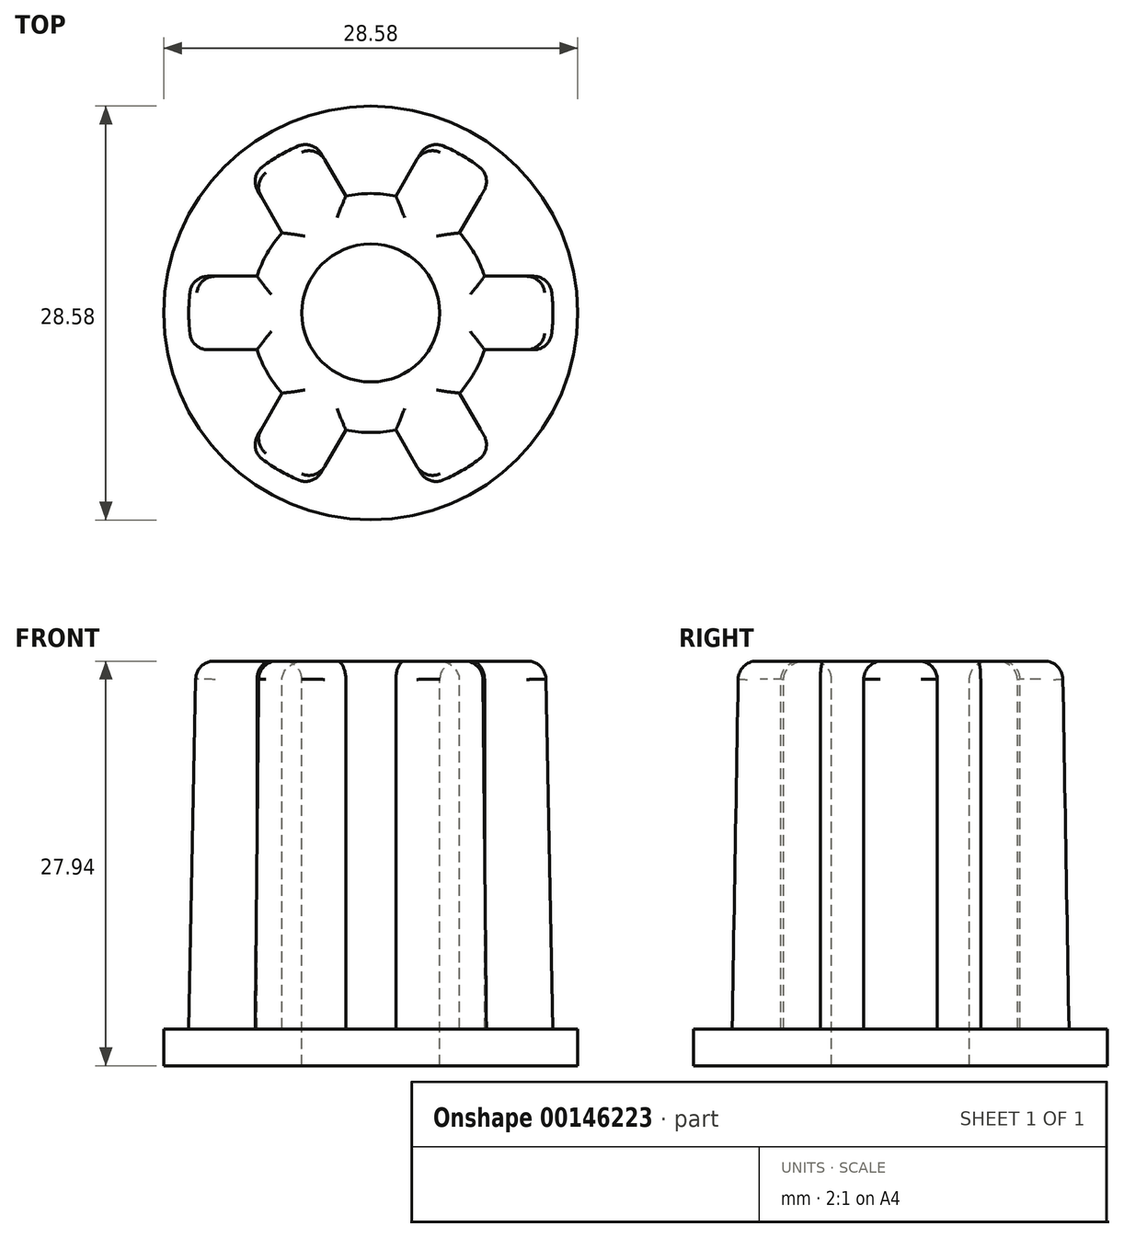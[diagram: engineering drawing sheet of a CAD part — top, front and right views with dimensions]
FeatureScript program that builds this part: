
annotation { "Feature Type Name" : "Feature", "Feature Type Description" : "" }
export const myFeature = defineFeature(function(context is Context, id is Id, definition is map)
    precondition{}
    {
        {
            var Q0;
            Q0=qCreatedBy(makeId("Top.planeOp"),FACE);
            var sketch = newSketch(context, id + "F0", { "sketchPlane" : qUnion([Q0])});
            skCircle(sketch, "E0", {"center": v(0, 0) * mm, "radius": 12.57 * mm});
            skSolve(sketch);
        }
        {
            var Q0;
            Q0=qCreatedBy(makeId("Top.planeOp"),FACE);
            cPlane(context, id + "F1", {"entities" : qUnion([Q0]), "cplaneType" : CPlaneType.OFFSET, "offset" : 25.4 * mm, "width" : 152.4 * mm, "height" : 152.4 * mm});
        }
        {
            var Q0;
            Q0=qCreatedBy(id+"F1.planeOp",FACE);
            var sketch = newSketch(context, id + "F2", { "sketchPlane" : qUnion([Q0])});
            skCircle(sketch, "E1", {"center": v(0, 0) * mm, "radius": 12.07 * mm});
            skSolve(sketch);
        }
        {
            var Q0;
            Q0=makeQuery(id+"F0.imprint","IMPRINT",FACE,{"disambiguationData":[TD([[makeQuery(id+"F0.imprint","IMPRINT",EDGE,{"derivedFrom":sQuery(id+"F0.wireOp",EDGE,"E0")}),1.0]])]});
            var Q1;
            Q1=makeQuery(id+"F2.imprint","IMPRINT",FACE,{"disambiguationData":[TD([[makeQuery(id+"F2.imprint","IMPRINT",EDGE,{"derivedFrom":sQuery(id+"F2.wireOp",EDGE,"E1")}),1.0]])]});
            loft(context, id + "F3", {"sheetProfilesArray" : [{ "sheetProfileEntities" : qUnion([Q0]) }, { "sheetProfileEntities" : qUnion([Q1]) }]});
        }
        {
            var Q0;
            Q0=makeQuery(id+"F3.opLoft","CAP_FACE",FACE,{"disambiguationData":[OSD([makeQuery(id+"F0.imprint","IMPRINT",FACE,{"disambiguationData":[TD([[makeQuery(id+"F0.imprint","IMPRINT",EDGE,{"derivedFrom":sQuery(id+"F0.wireOp",EDGE,"E0")}),1.0]])]})])],"isStart":true});
            var sketch = newSketch(context, id + "F4", { "sketchPlane" : qUnion([Q0])});
            skCircle(sketch, "E2", {"center": v(0, 0) * mm, "radius": 14.29 * mm});
            skSolve(sketch);
        }
        {
            var Q0;
            Q0 = qSketchRegion(id + "F4", true);
            extrude(context, id + "F5", {"entities" : qUnion([Q0]), "operationType" : NewBodyOperationType.ADD, "depth" : 2.54 * mm});
        }
        {
            var Q0;
            Q0=makeQuery(id+"F3.opLoft","CAP_FACE",FACE,{"disambiguationData":[OSD([makeQuery(id+"F2.imprint","IMPRINT",FACE,{"disambiguationData":[TD([[makeQuery(id+"F2.imprint","IMPRINT",EDGE,{"derivedFrom":sQuery(id+"F2.wireOp",EDGE,"E1")}),1.0]])]})])],"isStart":true});
            var sketch = newSketch(context, id + "F6", { "sketchPlane" : qUnion([Q0])});
            skCircle(sketch, "E3", {"center": v(0, 0) * mm, "radius": 4.76 * mm});
            skSolve(sketch);
        }
        {
            var Q0;
            Q0=sQuery(id+"F6.wireOp",VERTEX,"E3.center");
            var Q1;
            Q1=makeQuery(id+"F3.opLoft","SWEPT_BODY",BODY,{"disambiguationData":[OSD([makeQuery(id+"F0.imprint","IMPRINT",FACE,{"disambiguationData":[TD([[makeQuery(id+"F0.imprint","IMPRINT",EDGE,{"derivedFrom":sQuery(id+"F0.wireOp",EDGE,"E0")}),1.0]])]}),makeQuery(id+"F2.imprint","IMPRINT",FACE,{"disambiguationData":[TD([[makeQuery(id+"F2.imprint","IMPRINT",EDGE,{"derivedFrom":sQuery(id+"F2.wireOp",EDGE,"E1")}),1.0]])]})])]});
            hole(context, id + "F7", {"style" : HoleStyle.SIMPLE, "endStyle" : HoleEndStyle.THROUGH, "holeDiameter" : 9.52 * mm, "locations" : qUnion([Q0]), "scope" : qUnion([Q1]), "isTappedThrough" : true});
        }
        {
            var Q0;
            Q0=makeQuery(id+"F3.opLoft","CAP_FACE",FACE,{"disambiguationData":[OSD([makeQuery(id+"F2.imprint","IMPRINT",FACE,{"disambiguationData":[TD([[makeQuery(id+"F2.imprint","IMPRINT",EDGE,{"derivedFrom":sQuery(id+"F2.wireOp",EDGE,"E1")}),1.0]])]})])],"isStart":true});
            var sketch = newSketch(context, id + "F8", { "sketchPlane" : qUnion([Q0])});
            skArc(sketch, "E4", {"start": v(-6.13, 5.53) * mm, "mid": v(-7.15, 4.13) * mm, "end": v(-7.85, 2.54) * mm});
            skLineSegment(sketch, "E5.bottom", {"start": v(7.85, -2.54) * mm, "end": v(12.44, -2.54) * mm});
            skLineSegment(sketch, "E5.top", {"start": v(7.85, 2.54) * mm, "end": v(12.44, 2.54) * mm});
            skArc(sketch, "E6", {"start": v(-8.42, 9.5) * mm, "mid": v(-11, 6.35) * mm, "end": v(-12.44, 2.54) * mm});
            skLineSegment(sketch, "E7.1.0", {"start": v(1.73, 8.07) * mm, "end": v(4.02, 12.05) * mm});
            skLineSegment(sketch, "E7.1.1", {"start": v(6.13, 5.53) * mm, "end": v(8.42, 9.5) * mm});
            skLineSegment(sketch, "E7.2.0", {"start": v(-6.13, 5.53) * mm, "end": v(-8.42, 9.5) * mm});
            skLineSegment(sketch, "E7.2.1", {"start": v(-1.73, 8.07) * mm, "end": v(-4.02, 12.05) * mm});
            skLineSegment(sketch, "E7.3.0", {"start": v(-7.85, -2.54) * mm, "end": v(-12.44, -2.54) * mm});
            skLineSegment(sketch, "E7.3.1", {"start": v(-7.85, 2.54) * mm, "end": v(-12.44, 2.54) * mm});
            skLineSegment(sketch, "E7.4.0", {"start": v(-1.73, -8.07) * mm, "end": v(-4.02, -12.05) * mm});
            skLineSegment(sketch, "E7.4.1", {"start": v(-6.13, -5.53) * mm, "end": v(-8.42, -9.5) * mm});
            skLineSegment(sketch, "E7.5.0", {"start": v(6.13, -5.53) * mm, "end": v(8.42, -9.5) * mm});
            skLineSegment(sketch, "E7.5.1", {"start": v(1.73, -8.07) * mm, "end": v(4.02, -12.05) * mm});
            skArc(sketch, "E8.trimOffspring", {"start": v(1.73, 8.07) * mm, "mid": v(0, 8.26) * mm, "end": v(-1.73, 8.07) * mm});
            skArc(sketch, "E9.trimOffspring", {"start": v(4.02, 12.05) * mm, "mid": v(0, 12.7) * mm, "end": v(-4.02, 12.05) * mm});
            skArc(sketch, "E10.trimOffspring", {"start": v(-7.85, -2.54) * mm, "mid": v(-7.15, -4.13) * mm, "end": v(-6.13, -5.53) * mm});
            skArc(sketch, "E11.trimOffspring", {"start": v(-12.44, -2.54) * mm, "mid": v(-11, -6.35) * mm, "end": v(-8.42, -9.5) * mm});
            skArc(sketch, "E12.trimOffspring", {"start": v(-4.02, -12.05) * mm, "mid": v(0, -12.7) * mm, "end": v(4.02, -12.05) * mm});
            skArc(sketch, "E13.trimOffspring", {"start": v(-1.73, -8.07) * mm, "mid": v(0, -8.26) * mm, "end": v(1.73, -8.07) * mm});
            skArc(sketch, "E14.trimOffspring", {"start": v(6.13, -5.53) * mm, "mid": v(7.15, -4.13) * mm, "end": v(7.85, -2.54) * mm});
            skArc(sketch, "E15.trimOffspring", {"start": v(8.42, -9.5) * mm, "mid": v(11, -6.35) * mm, "end": v(12.44, -2.54) * mm});
            skArc(sketch, "E16.trimOffspring", {"start": v(12.44, 2.54) * mm, "mid": v(11, 6.35) * mm, "end": v(8.42, 9.5) * mm});
            skArc(sketch, "E17.trimOffspring", {"start": v(7.85, 2.54) * mm, "mid": v(7.15, 4.13) * mm, "end": v(6.13, 5.53) * mm});
            skSolve(sketch);
        }
        {
            var Q0;
            Q0 = qSketchRegion(id + "F8", true);
            extrude(context, id + "F9", {"entities" : qUnion([Q0]), "operationType" : NewBodyOperationType.REMOVE, "oppositeDirection" : true, "depth" : 25.4 * mm, "offsetDistance" : 25.4 * mm});
        }
        {
            var Q0;
            Q0=makeQuery(id+"F9.boolean.opBoolean","INTERSECT",EDGE,{"derivedFrom":[makeQuery(id+"F3.opLoft","SWEPT_FACE",FACE,{"disambiguationData":[OSD([sQuery(id+"F0.wireOp",EDGE,"E0"),sQuery(id+"F2.wireOp",EDGE,"E1")])]}),makeQuery(id+"F9.opExtrude","SWEPT_FACE",FACE,{"disambiguationData":[OSD([sQuery(id+"F8.wireOp",EDGE,"E7.3.0")])]})]});
            var Q1;
            Q1=makeQuery(id+"F9.boolean.opBoolean","INTERSECT",EDGE,{"derivedFrom":[makeQuery(id+"F3.opLoft","SWEPT_FACE",FACE,{"disambiguationData":[OSD([sQuery(id+"F0.wireOp",EDGE,"E0"),sQuery(id+"F2.wireOp",EDGE,"E1")])]}),makeQuery(id+"F9.opExtrude","SWEPT_FACE",FACE,{"disambiguationData":[OSD([sQuery(id+"F8.wireOp",EDGE,"E7.3.1")])]})]});
            var Q2;
            Q2=makeQuery(id+"F9.boolean.opBoolean","INTERSECT",EDGE,{"derivedFrom":[makeQuery(id+"F3.opLoft","SWEPT_FACE",FACE,{"disambiguationData":[OSD([sQuery(id+"F0.wireOp",EDGE,"E0"),sQuery(id+"F2.wireOp",EDGE,"E1")])]}),makeQuery(id+"F9.opExtrude","SWEPT_FACE",FACE,{"disambiguationData":[OSD([sQuery(id+"F8.wireOp",EDGE,"E7.4.1")])]})]});
            var Q3;
            Q3=makeQuery(id+"F9.boolean.opBoolean","INTERSECT",EDGE,{"derivedFrom":[makeQuery(id+"F3.opLoft","SWEPT_FACE",FACE,{"disambiguationData":[OSD([sQuery(id+"F0.wireOp",EDGE,"E0"),sQuery(id+"F2.wireOp",EDGE,"E1")])]}),makeQuery(id+"F9.opExtrude","SWEPT_FACE",FACE,{"disambiguationData":[OSD([sQuery(id+"F8.wireOp",EDGE,"E7.4.0")])]})]});
            var Q4;
            Q4=makeQuery(id+"F9.boolean.opBoolean","INTERSECT",EDGE,{"derivedFrom":[makeQuery(id+"F3.opLoft","SWEPT_FACE",FACE,{"disambiguationData":[OSD([sQuery(id+"F0.wireOp",EDGE,"E0"),sQuery(id+"F2.wireOp",EDGE,"E1")])]}),makeQuery(id+"F9.opExtrude","SWEPT_FACE",FACE,{"disambiguationData":[OSD([sQuery(id+"F8.wireOp",EDGE,"E7.5.1")])]})]});
            var Q5;
            Q5=makeQuery(id+"F9.boolean.opBoolean","INTERSECT",EDGE,{"derivedFrom":[makeQuery(id+"F3.opLoft","SWEPT_FACE",FACE,{"disambiguationData":[OSD([sQuery(id+"F0.wireOp",EDGE,"E0"),sQuery(id+"F2.wireOp",EDGE,"E1")])]}),makeQuery(id+"F9.opExtrude","SWEPT_FACE",FACE,{"disambiguationData":[OSD([sQuery(id+"F8.wireOp",EDGE,"E7.5.0")])]})]});
            var Q6;
            Q6=makeQuery(id+"F9.boolean.opBoolean","INTERSECT",EDGE,{"derivedFrom":[makeQuery(id+"F3.opLoft","SWEPT_FACE",FACE,{"disambiguationData":[OSD([sQuery(id+"F0.wireOp",EDGE,"E0"),sQuery(id+"F2.wireOp",EDGE,"E1")])]}),makeQuery(id+"F9.opExtrude","SWEPT_FACE",FACE,{"disambiguationData":[OSD([sQuery(id+"F8.wireOp",EDGE,"E5.bottom")])]})]});
            var Q7;
            Q7=makeQuery(id+"F9.boolean.opBoolean","INTERSECT",EDGE,{"derivedFrom":[makeQuery(id+"F3.opLoft","SWEPT_FACE",FACE,{"disambiguationData":[OSD([sQuery(id+"F0.wireOp",EDGE,"E0"),sQuery(id+"F2.wireOp",EDGE,"E1")])]}),makeQuery(id+"F9.opExtrude","SWEPT_FACE",FACE,{"disambiguationData":[OSD([sQuery(id+"F8.wireOp",EDGE,"E7.2.0")])]})]});
            var Q8;
            Q8=makeQuery(id+"F9.boolean.opBoolean","INTERSECT",EDGE,{"derivedFrom":[makeQuery(id+"F3.opLoft","SWEPT_FACE",FACE,{"disambiguationData":[OSD([sQuery(id+"F0.wireOp",EDGE,"E0"),sQuery(id+"F2.wireOp",EDGE,"E1")])]}),makeQuery(id+"F9.opExtrude","SWEPT_FACE",FACE,{"disambiguationData":[OSD([sQuery(id+"F8.wireOp",EDGE,"E7.2.1")])]})]});
            var Q9;
            Q9=makeQuery(id+"F9.boolean.opBoolean","INTERSECT",EDGE,{"derivedFrom":[makeQuery(id+"F3.opLoft","SWEPT_FACE",FACE,{"disambiguationData":[OSD([sQuery(id+"F0.wireOp",EDGE,"E0"),sQuery(id+"F2.wireOp",EDGE,"E1")])]}),makeQuery(id+"F9.opExtrude","SWEPT_FACE",FACE,{"disambiguationData":[OSD([sQuery(id+"F8.wireOp",EDGE,"E7.1.0")])]})]});
            var Q10;
            Q10=makeQuery(id+"F9.boolean.opBoolean","INTERSECT",EDGE,{"derivedFrom":[makeQuery(id+"F3.opLoft","SWEPT_FACE",FACE,{"disambiguationData":[OSD([sQuery(id+"F0.wireOp",EDGE,"E0"),sQuery(id+"F2.wireOp",EDGE,"E1")])]}),makeQuery(id+"F9.opExtrude","SWEPT_FACE",FACE,{"disambiguationData":[OSD([sQuery(id+"F8.wireOp",EDGE,"E7.1.1")])]})]});
            var Q11;
            Q11=makeQuery(id+"F9.boolean.opBoolean","INTERSECT",EDGE,{"derivedFrom":[makeQuery(id+"F3.opLoft","SWEPT_FACE",FACE,{"disambiguationData":[OSD([sQuery(id+"F0.wireOp",EDGE,"E0"),sQuery(id+"F2.wireOp",EDGE,"E1")])]}),makeQuery(id+"F9.opExtrude","SWEPT_FACE",FACE,{"disambiguationData":[OSD([sQuery(id+"F8.wireOp",EDGE,"E5.top")])]})]});
            var Q12;
            Q12=makeQuery(id+"F3.opLoft","CAP_FACE",FACE,{"disambiguationData":[OSD([makeQuery(id+"F2.imprint","IMPRINT",FACE,{"disambiguationData":[TD([[makeQuery(id+"F2.imprint","IMPRINT",EDGE,{"derivedFrom":sQuery(id+"F2.wireOp",EDGE,"E1")}),1.0]])]})])],"isStart":true});
            var Q13;
            Q13=makeQuery(id+"F7.hole-0.boolean.opBoolean","INTERSECT",EDGE,{"derivedFrom":[makeQuery(id+"F5.opExtrude","CAP_FACE",FACE,{"disambiguationData":[OSD([sQuery(id+"F4.wireOp",EDGE,"E2")])],"isStart":false}),makeQuery(id+"F7.hole-0.opRevolve","SWEPT_FACE",FACE,{"disambiguationData":[OSD([sQuery(id+"F7.hole-0.sketch.wireOp",EDGE,"core_line_2")])]})]});
            fillet(context, id + "F10", {"entities" : qUnion([Q0, Q1, Q2, Q3, Q4, Q5, Q6, Q7, Q8, Q9, Q10, Q11, Q12, Q13]), "radius" : 1.27 * mm, "tangentPropagation" : true, "allowEdgeOverflow" : false});
        }
    });
